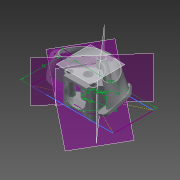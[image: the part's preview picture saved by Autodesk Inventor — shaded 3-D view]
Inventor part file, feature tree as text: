
AUTODESK INVENTOR PART (.ipt)
format: ipt  version: 2014 (Build 180170000, 170)  size: 1,568,256 bytes
history: native  units: mm
features: extrude x27, sketch x26, fillet x10, projected_geometry x9, chamfer x5, plane x5, loft x1, shell x1, mirror x1, boolean_combine x1
ambient origin geometry x8: Origin, YZ Plane, XZ Plane, XY Plane, X Axis, Y Axis, Z Axis, Center Point
bodies: Solid1 (feature_tree), Solid5 (feature_tree)
feature tree (86):
  sketch  "Sketch1"  dims[d0=12.0mm d2=10.0mm]
  extrude  "Extrusion1"  Depth=10.0mm
  extrude  "Extrusion2"  Depth=25.0mm
  extrude  "Extrusion3"  Depth=15.0mm
  extrude  "Extrusion6"  Depth=5.0mm TaperAngle=0.0deg
  extrude  "Extrusion7"  Depth=3.0mm
  extrude  "Extrusion8"  Depth=3.0mm
  extrude  "Extrusion9"  Depth=5.0mm TaperAngle=0.0deg
  extrude  "Extrusion10"  Depth=5.0mm
  extrude  "Extrusion11"  Depth=2.0mm
  fillet  "Fillet1"  [1 undecoded]
  fillet  "Fillet3"  Radius=2.0mm
  chamfer  "Chamfer1"  Distance=2.0mm
  extrude  "Extrusion12"  Depth=10.0mm TaperAngle=0.0deg
  chamfer  "Chamfer2"  Distance=2.0mm
  chamfer  "Chamfer3"  Distance=2.0mm Angle=45.0deg
  chamfer  "Chamfer4"  Distance=2.0mm
  fillet  "Fillet4"  Radius=2.5mm
  extrude  "Extrusion13"  Depth=2.0mm TaperAngle=0.0deg
  extrude  "Extrusion14"  Depth=4.0mm
  chamfer  "Chamfer5"  Distance=3.0mm
  plane  "Work Plane2"
  plane  "Work Plane1"
  sketch  "Sketch14"  dims[d40=10.0mm d41=0.0mm d42=10.0mm d43=0.0mm d44=2.0mm d45=0.0mm]
  sketch  "Sketch15"  dims[d47=0.125mm]
  sketch  "3D Sketch1"
  loft  "Loft7"
  shell  "Shell4"  Thickness=32.5mm
  extrude  "Extrusion23"  Depth=25.0mm
  mirror  "Mirror4"
  boolean_combine  "Combine4"
  extrude  "Extrusion24"  Depth=1.0mm
  extrude  "Extrusion25"  Depth=40.0mm
  extrude  "Extrusion26"  Depth=1.0mm
  extrude  "Extrusion27"  Depth=2.0mm
  plane  "Work Plane4"
  sketch  "Sketch33"  dims[d66=18.0mm d67=2.0mm d68=0.0mm]
  extrude  "Extrusion28"  Depth=2.0mm
  plane  "Work Plane5"
  sketch  "Sketch34"  dims[d69=4.0mm d70=4.0mm]
  extrude  "Extrusion29"  Depth=2.0mm
  extrude  "Extrusion31"  Depth=2.0mm
  extrude  "Extrusion32"  Depth=2.0mm
  extrude  "Extrusion33"  TaperAngle=90.0deg  [1 undecoded]
  extrude  "Extrusion34"  Depth=2.0mm
  extrude  "Extrusion35"  Depth=2.0mm
  extrude  "Extrusion36"  Depth=2.0mm
  fillet  "Fillet16"  Radius=3.0mm
  fillet  "Fillet17"  Radius=45.0mm
  fillet  "Fillet18"  Radius=45.0mm
  extrude  "Extrusion37"  Depth=2.0mm TaperAngle=0.0deg
  sketch  "Sketch42"  dims[d91=42.0mm d94=1.0mm]
  extrude  "Extrusion38"  Depth=2.0mm TaperAngle=0.0deg
  fillet  "Fillet19"  Radius=3.0mm
  fillet  "Fillet21"  Radius=20.0mm
  fillet  "Fillet22"  Radius=40.0mm
  fillet  "Fillet23"  Radius=3.0mm
  sketch  "Sketch2"  dims[d3=30.0mm d5=360.0deg d7=25.0mm]
  sketch  "Sketch4"  dims[d9=20.0mm d10=15.0mm]
  sketch  "Sketch6"  dims[d11=15.0mm d12=0.0mm d13=5.0mm d14=0.0mm]
  projected_geometry  "Projected Loop1"
  sketch  "Sketch7"  dims[d16=32.0mm d18=3.0mm]
  sketch  "Sketch8"  dims[d19=3.0mm d20=3.0mm]
  projected_geometry  "Projected Loop2"
  projected_geometry  "Projected Loop3"
  projected_geometry  "Projected Loop4"
  sketch  "Sketch10"  dims[d21=3.0mm d22=5.0mm d23=0.0mm]
  sketch  "Sketch11"  dims[d29=1.0mm d30=0.0mm d31=5.0mm]
  sketch  "Sketch12"  dims[d32=35.0mm d33=40.0mm d34=0.0mm d35=0.0mm d36=2.0mm d37=0.0mm d38=2.0mm d39=0.0mm]
  projected_geometry  "Projected Loop5"
  projected_geometry  "Projected Loop6"
  plane  "Work Plane3"
  sketch  "Sketch28"  dims[d49=2.5mm d50=5.0mm d51=2.0mm d52=45.0deg]
  sketch  "Sketch29"  dims[d53=15.0mm d54=2.0mm d55=0.0mm]
  sketch  "Sketch30"  dims[d56=8.0mm d57=2.0mm d58=45.0deg]
  sketch  "Sketch31"  dims[d59=10.0mm d60=2.0mm d61=45.0deg]
  sketch  "Sketch32"  dims[d62=2.0mm d63=2.0mm d64=45.0deg d65=2.5mm]
  projected_geometry  "Projected Loop10"
  sketch  "Sketch37"  dims[d71=4.0mm d72=3.0mm d73=0.0mm]
  sketch  "Sketch38"  dims[d74=1.5mm d75=2.0mm d76=45.0deg d78=14.0mm d79=32.5mm]
  sketch  "Sketch39"  dims[d80=55.0mm d81=25.0mm]
  sketch  "Sketch40"  dims[d82=15.0mm d83=1.0mm]
  sketch  "Sketch41"  dims[d84=11.0mm d87=40.0mm]
  sketch  "Sketch43"  dims[d95=1.0mm d96=1.0mm d97=1.0mm d98=1.0mm d99=0.5mm d129=50.0mm d130=90.0deg d160=15.0mm d162=135.0deg d180=0.0mm d181=90.0deg d182=0.0mm d183=90.0deg d189=32.0mm d190=32.0mm d191=3.0mm d192=45.0mm d193=45.0mm d194=4.0mm d195=0.0mm d197=3.0mm d198=0.0mm d199=3.0mm d200=0.0mm d201=20.0mm d202=40.0mm d203=3.0mm d204=0.0mm d205=3.0mm d206=0.0mm d207=30.0mm d208=5.0mm d209=3.0mm d210=0.0mm d211=30.0mm d212=5.0mm d213=3.0mm d214=0.0mm d217=3.0mm d218=0.0mm d219=3.0mm d220=0.0mm d221=3.0mm d222=0.0mm d223=3.0mm d224=0.0mm d225=4.0mm d226=0.0mm d227=4.0mm d228=0.0mm d229=2.0mm d230=2.0mm d231=5.0mm d232=15.0mm d233=3.0mm d234=0.0mm d235=155.0mm d236=75.0mm d238=50.0mm d239=0.0mm d240=10.0mm d242=2.5mm d243=2.5mm d244=3.5mm d246=1.0mm d247=2.0mm d248=1.5mm]
  projected_geometry  "Projected Loop11"
  projected_geometry  "Project Cut Edges1"
note: 2 required parameter values undecoded (feature->parameter linkage not recoverable at this tier; creation-order binding heuristic only, values carry confidence <= 0.55)
